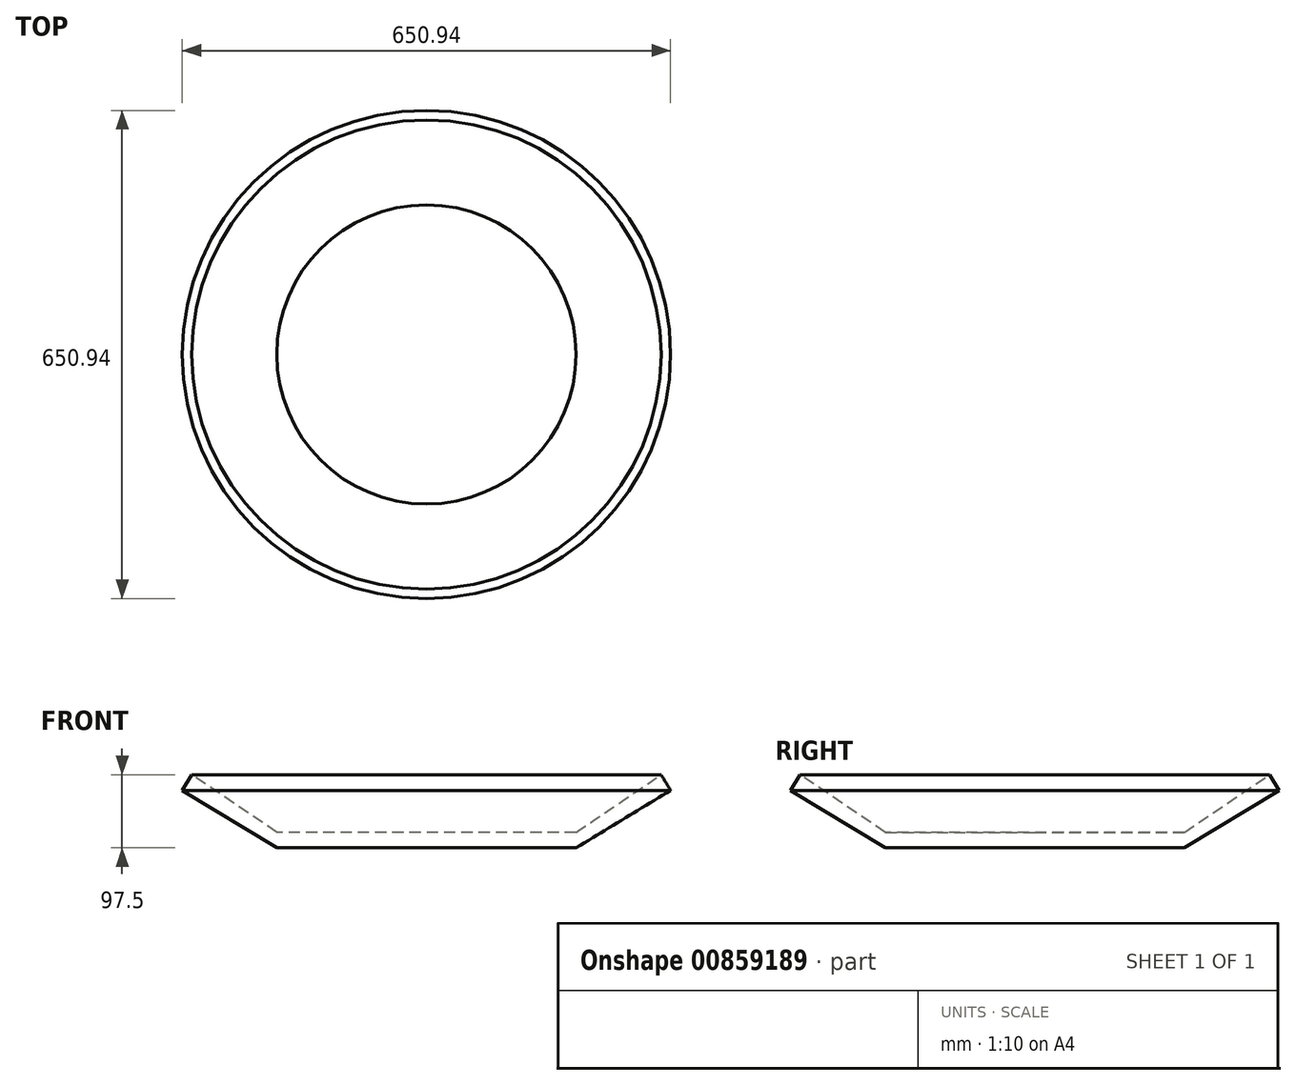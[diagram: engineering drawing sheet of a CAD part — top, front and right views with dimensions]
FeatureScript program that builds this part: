
annotation { "Feature Type Name" : "Feature", "Feature Type Description" : "" }
export const myFeature = defineFeature(function(context is Context, id is Id, definition is map)
    precondition{}
    {
        {
            var Q0;
            Q0=qCreatedBy(makeId("Front.planeOp"),FACE);
            var sketch = newSketch(context, id + "F0", { "sketchPlane" : qUnion([Q0])});
            skLineSegment(sketch, "E0.bottom", {"start": v(0, -55.96) * mm, "end": v(-199.45, -55.96) * mm});
            skLineSegment(sketch, "E0.top", {"start": v(0, -76.67) * mm, "end": v(-199.45, -76.67) * mm});
            skLineSegment(sketch, "E0.left", {"start": v(0, -55.96) * mm, "end": v(0, -76.67) * mm});
            skLineSegment(sketch, "E0.right", {"start": v(-199.45, -55.96) * mm, "end": v(-199.45, -76.67) * mm});
            skLineSegment(sketch, "E1", {"start": v(-199.45, -76.67) * mm, "end": v(-325.47, 0) * mm});
            skLineSegment(sketch, "E2", {"start": v(-325.47, 0) * mm, "end": v(-312.8, 20.83) * mm});
            skLineSegment(sketch, "E3", {"start": v(-312.8, 20.83) * mm, "end": v(-199.45, -55.96) * mm});
            skSolve(sketch);
        }
        {
            var Q0;
            Q0 = qSketchRegion(id + "F0", true);
            var Q1;
            Q1=sQuery(id+"F0.wireOp",EDGE,"E0.left");
            revolve(context, id + "F1", {"surfaceOperationType" : NewSurfaceOperationType.NEW, "entities" : qUnion([Q0]), "axis" : qUnion([Q1]), "revolveType" : RevolveType.FULL});
        }
    });
